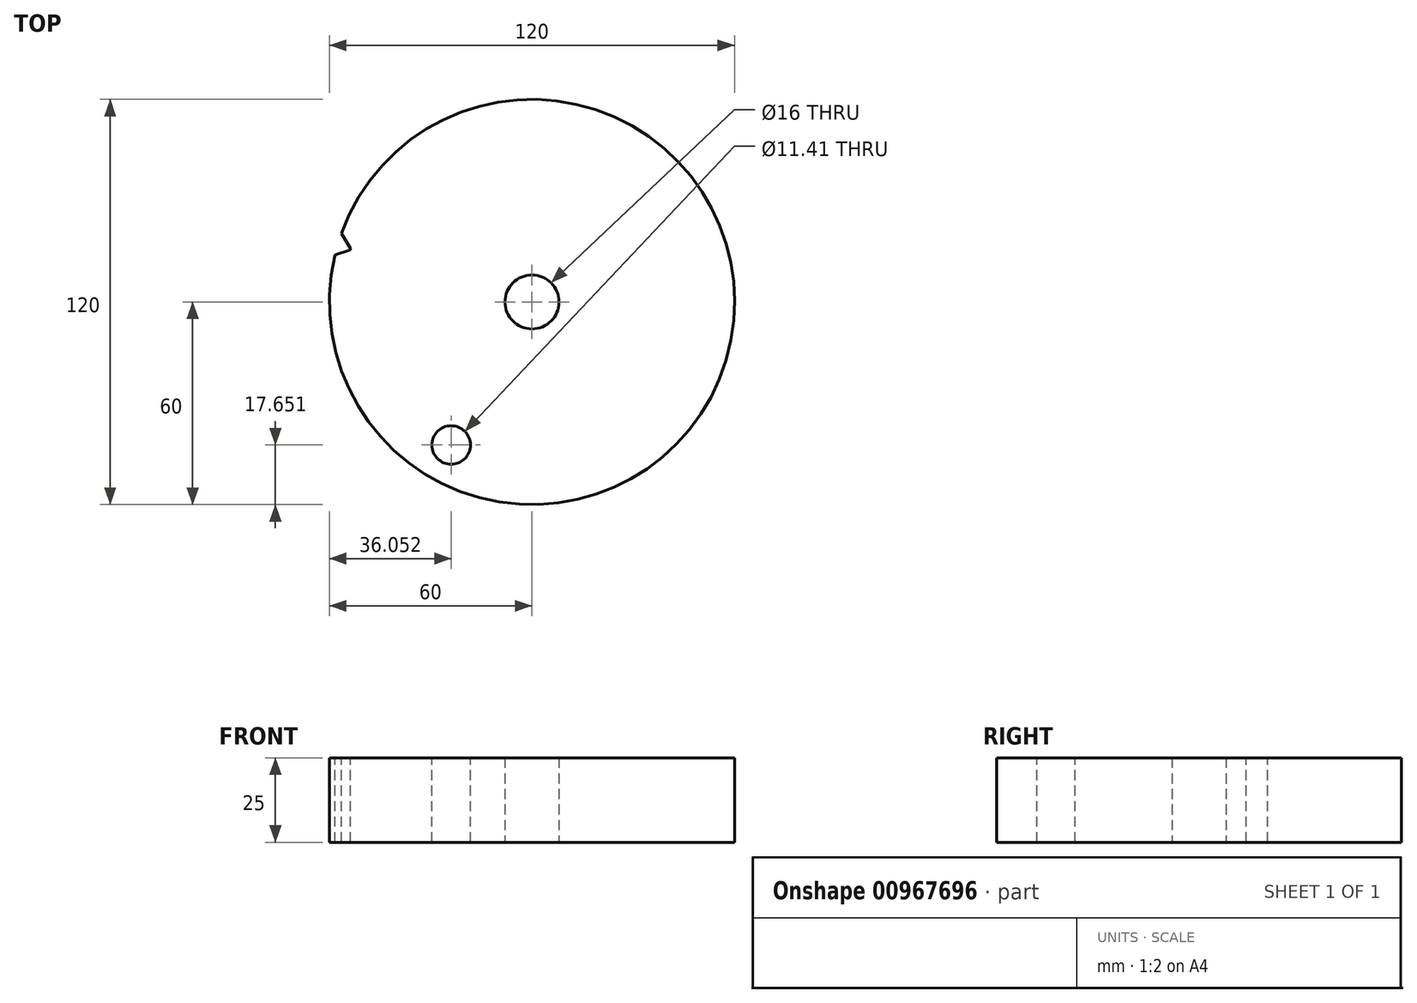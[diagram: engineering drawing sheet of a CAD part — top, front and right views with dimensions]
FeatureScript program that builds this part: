
annotation { "Feature Type Name" : "Feature", "Feature Type Description" : "" }
export const myFeature = defineFeature(function(context is Context, id is Id, definition is map)
    precondition{}
    {
        {
            var Q0;
            Q0=qCreatedBy(makeId("Top.planeOp"),FACE);
            var sketch = newSketch(context, id + "F0", { "sketchPlane" : qUnion([Q0])});
            skCircle(sketch, "E0", {"center": v(0, 0) * mm, "radius": 60 * mm});
            skCircle(sketch, "E1", {"center": v(0, 0) * mm, "radius": 8 * mm});
            skCircle(sketch, "E2", {"center": v(0, 0) * mm, "radius": 53 * mm});
            skLineSegment(sketch, "E3", {"start": v(1.28, 59.99) * mm, "end": v(4.37, 52.82) * mm});
            skLineSegment(sketch, "E4", {"start": v(4.37, 52.82) * mm, "end": v(8.6, 59.38) * mm});
            skSolve(sketch);
        }
        {
            var Q0;
            Q0 = qSketchRegion(id + "F0", true);
            var Q1;
            Q1=makeQuery(id+"F0.imprint","IMPRINT",FACE,{"disambiguationData":[TD([[makeQuery(id+"F0.imprint","IMPRINT",EDGE,{"derivedFrom":sQuery(id+"F0.wireOp",EDGE,"E1")}),-1.0]])]});
            extrude(context, id + "F1", {"entities" : qUnion([Q0, Q1]), "depth" : 25 * mm, "offsetDistance" : 25 * mm});
        }
        {
            var Q0;
            Q0=makeQuery(id+"F1.opExtrude","CAP_FACE",FACE,{"disambiguationData":[OSD([sQuery(id+"F0.wireOp",EDGE,"E0"),sQuery(id+"F0.wireOp",EDGE,"E1")])],"isStart":false});
            var sketch = newSketch(context, id + "F2", { "sketchPlane" : qUnion([Q0])});
            skCircle(sketch, "E5", {"center": v(-23.95, -42.35) * mm, "radius": 5.7 * mm});
            skSolve(sketch);
        }
        {
            var Q0;
            Q0 = qSketchRegion(id + "F2", true);
            extrude(context, id + "F3", {"entities" : qUnion([Q0]), "operationType" : NewBodyOperationType.REMOVE, "endBound" : BoundingType.THROUGH_ALL, "oppositeDirection" : true, "depth" : 25 * mm, "offsetDistance" : 25 * mm});
        }
        {
            var Q0;
            Q0=makeQuery(id+"F1.opExtrude","CAP_FACE",FACE,{"disambiguationData":[OSD([sQuery(id+"F0.wireOp",EDGE,"E0"),sQuery(id+"F0.wireOp",EDGE,"E1")])],"isStart":false});
            var sketch = newSketch(context, id + "F4", { "sketchPlane" : qUnion([Q0])});
            skLineSegment(sketch, "E6", {"start": v(-58.36, 13.92) * mm, "end": v(-54.01, 15.3) * mm});
            skLineSegment(sketch, "E7", {"start": v(-53.8, 15.9) * mm, "end": v(-56.44, 20.36) * mm});
            skPoint(sketch, "E8.visualSharp", {"position": v(-53.53, 15.46) * mm});
            skArc(sketch, "E8.filletArc", {"start": v(-54.01, 15.3) * mm, "mid": v(-53.76, 15.55) * mm, "end": v(-53.8, 15.9) * mm});
            skSolve(sketch);
        }
        {
            var Q0;
            {var subQ0=sQuery(id+"F4.wireOp",EDGE,"E6");Q0=makeQuery(id+"F4.imprint","IMPRINT",FACE,{"disambiguationData":[TD([[makeQuery(id+"F4.imprint","IMPRINT",EDGE,{"derivedFrom":subQ0}),1.0]])]});}
            extrude(context, id + "F5", {"entities" : qUnion([Q0]), "operationType" : NewBodyOperationType.REMOVE, "endBound" : BoundingType.THROUGH_ALL, "oppositeDirection" : true, "depth" : 25 * mm, "offsetDistance" : 25 * mm});
        }
    });
